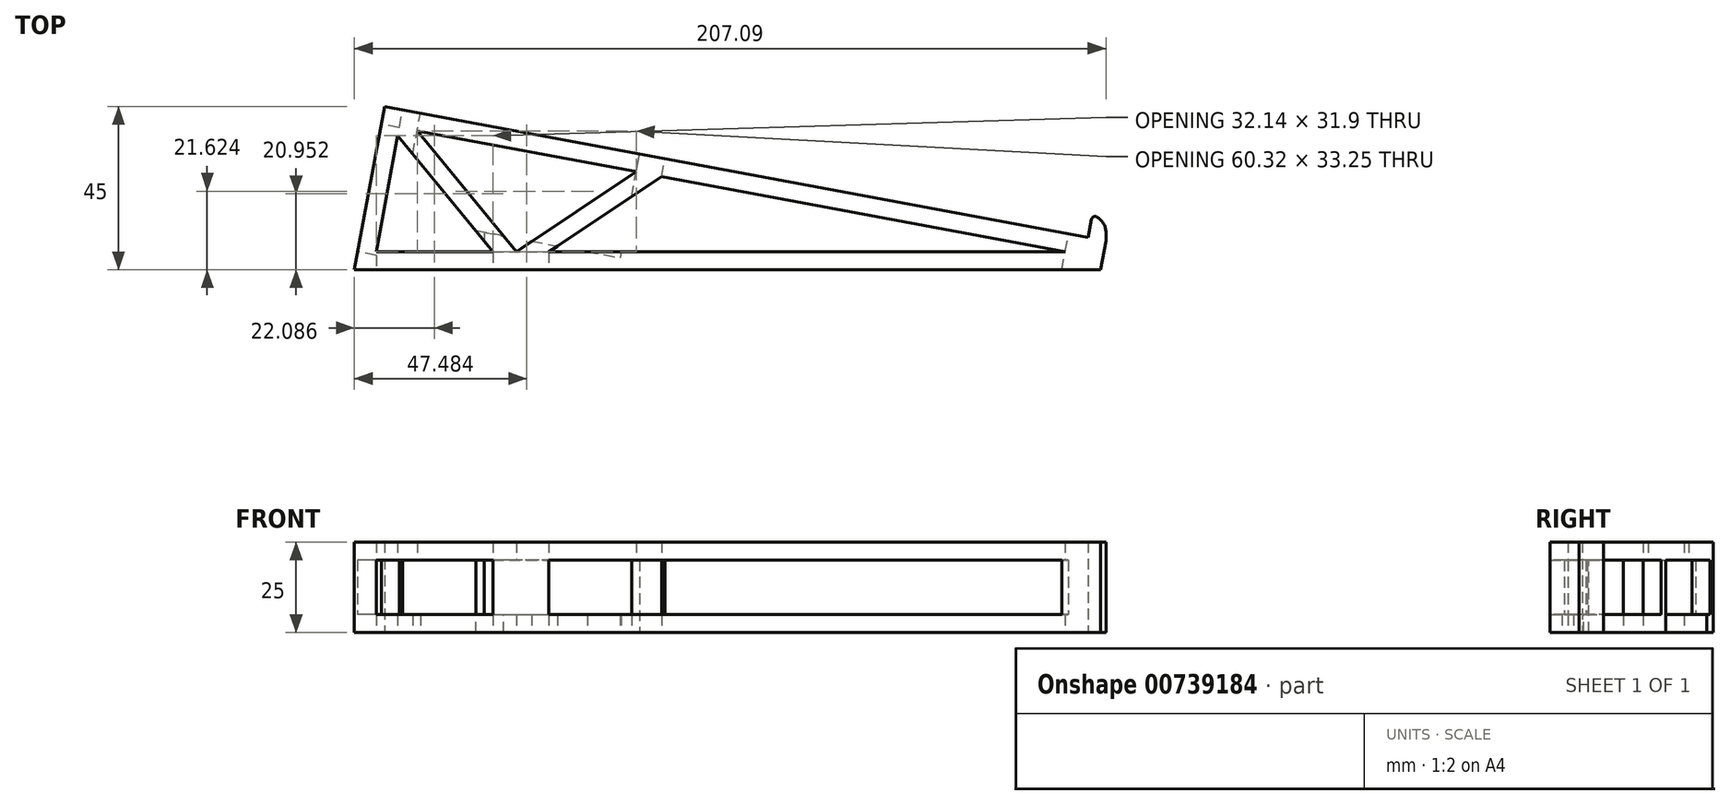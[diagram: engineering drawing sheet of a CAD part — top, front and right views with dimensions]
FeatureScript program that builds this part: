
annotation { "Feature Type Name" : "Feature", "Feature Type Description" : "" }
export const myFeature = defineFeature(function(context is Context, id is Id, definition is map)
    precondition{}
    {
        {
            var Q0;
            Q0=qCreatedBy(makeId("Top.planeOp"),FACE);
            var sketch = newSketch(context, id + "F0", { "sketchPlane" : qUnion([Q0])});
            skLineSegment(sketch, "E0", {"start": v(-65.8, 0) * mm, "end": v(184.2, 0) * mm});
            skLineSegment(sketch, "E1", {"start": v(184.2, 0) * mm, "end": v(-57.41, 45) * mm});
            skLineSegment(sketch, "E2", {"start": v(-57.41, 45) * mm, "end": v(-65.8, 0) * mm});
            skLineSegment(sketch, "E3", {"start": v(179.4, 0.9) * mm, "end": v(180.54, 7.05) * mm});
            skLineSegment(sketch, "E4", {"start": v(180.54, 7.05) * mm, "end": v(184.2, 0) * mm});
            skLineSegment(sketch, "E5.0", {"start": v(130.05, 5) * mm, "end": v(-53.41, 39.17) * mm});
            skLineSegment(sketch, "E5.1", {"start": v(-59.78, 5) * mm, "end": v(130.05, 5) * mm});
            skLineSegment(sketch, "E5.2", {"start": v(-53.41, 39.17) * mm, "end": v(-59.78, 5) * mm});
            skLineSegment(sketch, "E6", {"start": v(139.8, 0) * mm, "end": v(141.3, 8) * mm});
            skLineSegment(sketch, "E7", {"start": v(141.3, 8) * mm, "end": v(141.3, 14.36) * mm});
            skLineSegment(sketch, "E8", {"start": v(141.3, 14.36) * mm, "end": v(137.53, 15.06) * mm});
            skLineSegment(sketch, "E9", {"start": v(137.53, 15.06) * mm, "end": v(136.38, 8.9) * mm});
            skLineSegment(sketch, "E10", {"start": v(-57.41, 45) * mm, "end": v(-57.41, 0) * mm, "construction": true});
            skLineSegment(sketch, "E11", {"start": v(-53.83, 36.9) * mm, "end": v(-27.63, 5) * mm});
            skLineSegment(sketch, "E12", {"start": v(-48.47, 38.25) * mm, "end": v(-21.16, 5) * mm});
            skLineSegment(sketch, "E13", {"start": v(-40.73, 20.95) * mm, "end": v(-36.87, 24.13) * mm, "construction": true});
            skLineSegment(sketch, "E14", {"start": v(-21.16, 5) * mm, "end": v(11.86, 27.01) * mm});
            skLineSegment(sketch, "E15", {"start": v(-12.15, 5) * mm, "end": v(18.9, 25.7) * mm});
            skLineSegment(sketch, "E16", {"start": v(-3.69, 16.65) * mm, "end": v(-0.92, 12.49) * mm, "construction": true});
            skSolve(sketch);
        }
        {
            var Q0;
            {var subQ0=sQuery(id+"F0.wireOp",EDGE,"E2");Q0=makeQuery(id+"F0.imprint","IMPRINT",FACE,{"disambiguationData":[TD([[makeQuery(id+"F0.imprint","IMPRINT",EDGE,{"derivedFrom":subQ0}),1.0]])]});}
            var Q1;
            {var subQ0=sQuery(id+"F0.wireOp",EDGE,"E7");Q1=makeQuery(id+"F0.imprint","IMPRINT",FACE,{"disambiguationData":[TD([[makeQuery(id+"F0.imprint","IMPRINT",EDGE,{"derivedFrom":subQ0}),1.0]])]});}
            var Q2;
            {var subQ0=sQuery(id+"F0.wireOp",EDGE,"E11");Q2=makeQuery(id+"F0.imprint","IMPRINT",FACE,{"disambiguationData":[TD([[makeQuery(id+"F0.imprint","IMPRINT",EDGE,{"derivedFrom":subQ0}),1.0]])]});}
            var Q3;
            {var subQ0=sQuery(id+"F0.wireOp",EDGE,"E14");Q3=makeQuery(id+"F0.imprint","IMPRINT",FACE,{"disambiguationData":[TD([[makeQuery(id+"F0.imprint","IMPRINT",EDGE,{"derivedFrom":subQ0}),-1.0]])]});}
            extrude(context, id + "F1", {"entities" : qUnion([Q0, Q1, Q2, Q3]), "depth" : 25 * mm, "offsetDistance" : 25 * mm});
        }
        {
            var Q0;
            Q0=makeQuery(id+"F1.opExtrude","SWEPT_FACE",FACE,{"disambiguationData":[OSD([sQuery(id+"F0.wireOp",EDGE,"E1")])]});
            cPlane(context, id + "F2", {"entities" : qUnion([Q0]), "cplaneType" : CPlaneType.OFFSET, "offset" : 0 * mm, "width" : 150 * mm, "height" : 150 * mm});
        }
        {
            var Q0;
            Q0=qCreatedBy(id+"F2.planeOp",FACE);
            var sketch = newSketch(context, id + "F3", { "sketchPlane" : qUnion([Q0])});
            skPoint(sketch, "E17.0", {"position": v(-126.94, 25) * mm});
            skPoint(sketch, "E17.1", {"position": v(-126.94, 0) * mm});
            skPoint(sketch, "E17.2", {"position": v(-13.88, 0) * mm});
            skPoint(sketch, "E17.3", {"position": v(-6.7, 0) * mm});
            skPoint(sketch, "E17.4", {"position": v(-13.88, 25) * mm});
            skPoint(sketch, "E17.5", {"position": v(-6.7, 25) * mm});
            skPoint(sketch, "E17.6", {"position": v(54.65, 25) * mm});
            skPoint(sketch, "E17.7", {"position": v(54.65, 0) * mm});
            skLineSegment(sketch, "E18.bottom", {"start": v(-126.94, 25) * mm, "end": v(-13.88, 25) * mm});
            skLineSegment(sketch, "E18.top", {"start": v(-126.94, 0) * mm, "end": v(-13.88, 0) * mm});
            skLineSegment(sketch, "E18.left", {"start": v(-126.94, 25) * mm, "end": v(-126.94, 0) * mm});
            skLineSegment(sketch, "E18.right", {"start": v(-13.88, 25) * mm, "end": v(-13.88, 0) * mm});
            skLineSegment(sketch, "E19.bottom", {"start": v(-6.7, 25) * mm, "end": v(54.65, 25) * mm});
            skLineSegment(sketch, "E19.top", {"start": v(-6.7, 0) * mm, "end": v(54.65, 0) * mm});
            skLineSegment(sketch, "E19.left", {"start": v(-6.7, 25) * mm, "end": v(-6.7, 0) * mm});
            skLineSegment(sketch, "E19.right", {"start": v(54.65, 25) * mm, "end": v(54.65, 0) * mm});
            skLineSegment(sketch, "E20.0", {"start": v(-121.94, 20) * mm, "end": v(-18.88, 20) * mm});
            skLineSegment(sketch, "E20.1", {"start": v(-121.94, 20) * mm, "end": v(-121.94, 5) * mm});
            skLineSegment(sketch, "E20.2", {"start": v(-121.94, 5) * mm, "end": v(-18.88, 5) * mm});
            skLineSegment(sketch, "E20.3", {"start": v(-18.88, 20) * mm, "end": v(-18.88, 5) * mm});
            skLineSegment(sketch, "E21.0", {"start": v(-1.7, 20) * mm, "end": v(-1.7, 5) * mm});
            skLineSegment(sketch, "E21.1", {"start": v(-1.7, 20) * mm, "end": v(49.65, 20) * mm});
            skLineSegment(sketch, "E21.2", {"start": v(49.65, 20) * mm, "end": v(49.65, 5) * mm});
            skLineSegment(sketch, "E21.3", {"start": v(-1.7, 5) * mm, "end": v(49.65, 5) * mm});
            skLineSegment(sketch, "E22", {"start": v(-1.7, 20) * mm, "end": v(-6.7, 20) * mm});
            skLineSegment(sketch, "E23", {"start": v(0, 5) * mm, "end": v(-1.7, 5) * mm});
            skLineSegment(sketch, "E24", {"start": v(-18.88, 20) * mm, "end": v(-13.88, 20) * mm});
            skLineSegment(sketch, "E25", {"start": v(-18.88, 5) * mm, "end": v(-13.88, 5) * mm});
            skLineSegment(sketch, "E26", {"start": v(49.65, 5) * mm, "end": v(54.65, 5) * mm});
            skLineSegment(sketch, "E27", {"start": v(49.65, 20) * mm, "end": v(54.65, 20) * mm});
            skLineSegment(sketch, "E28", {"start": v(-121.94, 20) * mm, "end": v(-126.94, 20) * mm});
            skLineSegment(sketch, "E29", {"start": v(-121.94, 5) * mm, "end": v(-126.94, 5) * mm});
            skPoint(sketch, "E30.0", {"position": v(59.68, 25) * mm});
            skLineSegment(sketch, "E31", {"start": v(59.68, 25) * mm, "end": v(59.68, 0) * mm});
            skLineSegment(sketch, "E32", {"start": v(54.65, 5) * mm, "end": v(59.68, 5) * mm});
            skLineSegment(sketch, "E33", {"start": v(54.65, 20) * mm, "end": v(59.68, 20) * mm});
            skSolve(sketch);
        }
        {
            var Q0;
            Q0=makeQuery(id+"F3.imprint","IMPRINT",FACE,{"disambiguationData":[TD([[makeQuery(id+"F3.imprint","IMPRINT",EDGE,{"derivedFrom":sQuery(id+"F3.wireOp",EDGE,"E20.0")}),-1.0]])]});
            var Q1;
            Q1=makeQuery(id+"F3.imprint","IMPRINT",FACE,{"disambiguationData":[TD([[makeQuery(id+"F3.imprint","IMPRINT",EDGE,{"derivedFrom":sQuery(id+"F3.wireOp",EDGE,"E21.0")}),1.0]])]});
            var Q2;
            Q2=makeQuery(id+"F3.imprint","IMPRINT",FACE,{"disambiguationData":[TD([[makeQuery(id+"F3.imprint","IMPRINT",EDGE,{"derivedFrom":sQuery(id+"F3.wireOp",EDGE,"E20.1")}),-1.0]])]});
            var Q3;
            Q3=makeQuery(id+"F3.imprint","IMPRINT",FACE,{"disambiguationData":[TD([[makeQuery(id+"F3.imprint","IMPRINT",EDGE,{"derivedFrom":sQuery(id+"F3.wireOp",EDGE,"E20.3")}),1.0]])]});
            var Q4;
            {var subQ4=sQuery(id+"F3.wireOp",EDGE,"E21.0");Q4=makeQuery(id+"F3.imprint","IMPRINT",FACE,{"disambiguationData":[TD([[makeQuery(id+"F3.imprint","IMPRINT",EDGE,{"derivedFrom":subQ4}),-1.0]])]});}
            var Q5;
            Q5=makeQuery(id+"F3.imprint","IMPRINT",FACE,{"disambiguationData":[TD([[makeQuery(id+"F3.imprint","IMPRINT",EDGE,{"derivedFrom":sQuery(id+"F3.wireOp",EDGE,"E21.2")}),1.0]])]});
            var Q6;
            {var subQ0=sQuery(id+"F3.wireOp",EDGE,"E32");Q6=makeQuery(id+"F3.imprint","IMPRINT",FACE,{"disambiguationData":[TD([[makeQuery(id+"F3.imprint","IMPRINT",EDGE,{"derivedFrom":subQ0}),1.0]])]});}
            extrude(context, id + "F4", {"entities" : qUnion([Q0, Q1, Q2, Q3, Q4, Q5, Q6]), "operationType" : NewBodyOperationType.REMOVE, "oppositeDirection" : true, "depth" : 29.1 * mm, "offsetDistance" : 25 * mm});
        }
        {
            var Q0;
            Q0=qCreatedBy(makeId("Front.planeOp"),FACE);
            var sketch = newSketch(context, id + "F5", { "sketchPlane" : qUnion([Q0])});
            skPoint(sketch, "E34.0", {"position": v(-12.15, 25) * mm});
            skPoint(sketch, "E34.1", {"position": v(-27.63, 25) * mm});
            skPoint(sketch, "E34.2", {"position": v(-59.78, 25) * mm});
            skPoint(sketch, "E35.0", {"position": v(25.27, 5) * mm});
            skPoint(sketch, "E36.0", {"position": v(25.27, 20) * mm});
            skLineSegment(sketch, "E37", {"start": v(25.27, 5) * mm, "end": v(-59.78, 5) * mm});
            skLineSegment(sketch, "E38", {"start": v(25.27, 20) * mm, "end": v(-59.78, 20) * mm});
            skLineSegment(sketch, "E39", {"start": v(-59.78, 25) * mm, "end": v(-59.78, 5) * mm});
            skLineSegment(sketch, "E40", {"start": v(-27.63, 25) * mm, "end": v(-27.63, 5) * mm});
            skLineSegment(sketch, "E41", {"start": v(-12.15, 25) * mm, "end": v(-12.15, 5) * mm});
            skLineSegment(sketch, "E42", {"start": v(25.27, 5) * mm, "end": v(25.27, 20) * mm});
            skSolve(sketch);
        }
        {
            var Q0;
            {var subQ0=sQuery(id+"F5.wireOp",EDGE,"E39");var subQ1=sQuery(id+"F5.wireOp",EDGE,"E37");var subQ2=makeQuery(id+"F5.imprint","INTERSECT",VERTEX,{"derivedFrom":[subQ1,subQ0]});Q0=makeQuery(id+"F5.imprint","IMPRINT",FACE,{"disambiguationData":[TD([[makeQuery(id+"F5.imprint","IMPRINT",EDGE,{"disambiguationData":[TD([[subQ2,1.0]])],"derivedFrom":subQ1}),-1.0]])]});}
            var Q1;
            {var subQ0=sQuery(id+"F5.wireOp",EDGE,"E42");Q1=makeQuery(id+"F5.imprint","IMPRINT",FACE,{"disambiguationData":[TD([[makeQuery(id+"F5.imprint","IMPRINT",EDGE,{"derivedFrom":subQ0}),1.0]])]});}
            extrude(context, id + "F6", {"entities" : qUnion([Q0, Q1]), "operationType" : NewBodyOperationType.REMOVE, "oppositeDirection" : true, "depth" : 5 * mm, "offsetDistance" : 25 * mm});
        }
        {
            var Q0;
            Q0=makeQuery(id+"F1.opExtrude","SWEPT_FACE",FACE,{"disambiguationData":[OSD([sQuery(id+"F0.wireOp",EDGE,"E2")])]});
            cPlane(context, id + "F7", {"entities" : qUnion([Q0]), "cplaneType" : CPlaneType.OFFSET, "offset" : 0 * mm, "width" : 150 * mm, "height" : 150 * mm});
        }
        {
            var Q0;
            Q0=qCreatedBy(id+"F7.planeOp",FACE);
            var sketch = newSketch(context, id + "F8", { "sketchPlane" : qUnion([Q0])});
            skLineSegment(sketch, "E43.0", {"start": v(-33.73, 0) * mm, "end": v(12.05, 0) * mm});
            skLineSegment(sketch, "E44.0", {"start": v(-33.73, 25) * mm, "end": v(-33.73, 0) * mm});
            skLineSegment(sketch, "E45.0", {"start": v(-33.73, 25) * mm, "end": v(12.05, 25) * mm});
            skLineSegment(sketch, "E46.0", {"start": v(12.05, 25) * mm, "end": v(12.05, 0) * mm});
            skLineSegment(sketch, "E47.0", {"start": v(7.05, 20) * mm, "end": v(7.05, 5) * mm});
            skLineSegment(sketch, "E47.1", {"start": v(-28.73, 20) * mm, "end": v(7.05, 20) * mm});
            skLineSegment(sketch, "E47.2", {"start": v(-28.73, 20) * mm, "end": v(-28.73, 5) * mm});
            skLineSegment(sketch, "E47.3", {"start": v(-28.73, 5) * mm, "end": v(7.05, 5) * mm});
            skSolve(sketch);
        }
        {
            var Q0;
            Q0=makeQuery(id+"F8.imprint","IMPRINT",FACE,{"disambiguationData":[TD([[makeQuery(id+"F8.imprint","IMPRINT",EDGE,{"derivedFrom":sQuery(id+"F8.wireOp",EDGE,"E47.0")}),-1.0]])]});
            extrude(context, id + "F9", {"entities" : qUnion([Q0]), "operationType" : NewBodyOperationType.REMOVE, "oppositeDirection" : true, "depth" : 25 * mm, "offsetDistance" : 25 * mm});
        }
        {
            var Q0;
            Q0=makeQuery(id+"F1.opExtrude","SWEPT_EDGE",EDGE,{"disambiguationData":[OSD([sQuery(id+"F0.wireOp",EDGE,"E7"),sQuery(id+"F0.wireOp",EDGE,"E8")])]});
            fillet(context, id + "F10", {"entities" : qUnion([Q0]), "radius" : 5 * mm, "tangentPropagation" : true, "allowEdgeOverflow" : false});
        }
        {
            var Q0;
            Q0=makeQuery(id+"F10.opFillet","BLEND_EDGE",EDGE,{"blendedFrom":[makeQuery(id+"F1.opExtrude","SWEPT_EDGE",EDGE,{"disambiguationData":[OSD([sQuery(id+"F0.wireOp",EDGE,"E7"),sQuery(id+"F0.wireOp",EDGE,"E8")])]}),makeQuery(id+"F1.opExtrude","SWEPT_FACE",FACE,{"disambiguationData":[OSD([sQuery(id+"F0.wireOp",EDGE,"E9")])]})],"blendedInto":[makeQuery(id+"F1.opExtrude","SWEPT_FACE",FACE,{"disambiguationData":[OSD([sQuery(id+"F0.wireOp",EDGE,"E9")])]})]});
            fillet(context, id + "F11", {"entities" : qUnion([Q0]), "radius" : 1 * mm, "tangentPropagation" : true, "allowEdgeOverflow" : false});
        }
        {
            var Q0;
            Q0=qCreatedBy(makeId("Right.planeOp"),FACE);
            var sketch = newSketch(context, id + "F12", { "sketchPlane" : qUnion([Q0])});
            skPoint(sketch, "E48.0", {"position": v(4.92, 5) * mm});
            skLineSegment(sketch, "E48.1", {"start": v(4.92, 20) * mm, "end": v(4.92, 5) * mm});
            skLineSegment(sketch, "E48.2", {"start": v(40.08, 20) * mm, "end": v(4.92, 20) * mm});
            skLineSegment(sketch, "E48.3", {"start": v(40.08, 5) * mm, "end": v(4.92, 5) * mm});
            skLineSegment(sketch, "E49.0", {"start": v(20.15, 20) * mm, "end": v(20.15, 0) * mm});
            skSolve(sketch);
        }
        {
            var Q0;
            {var subQ0=sQuery(id+"F12.wireOp",EDGE,"E48.1");Q0=makeQuery(id+"F12.imprint","IMPRINT",FACE,{"disambiguationData":[TD([[makeQuery(id+"F12.imprint","IMPRINT",EDGE,{"derivedFrom":subQ0}),1.0]])]});}
            extrude(context, id + "F13", {"entities" : qUnion([Q0]), "operationType" : NewBodyOperationType.REMOVE, "oppositeDirection" : true, "depth" : 30 * mm, "offsetDistance" : 25 * mm});
        }
    });
